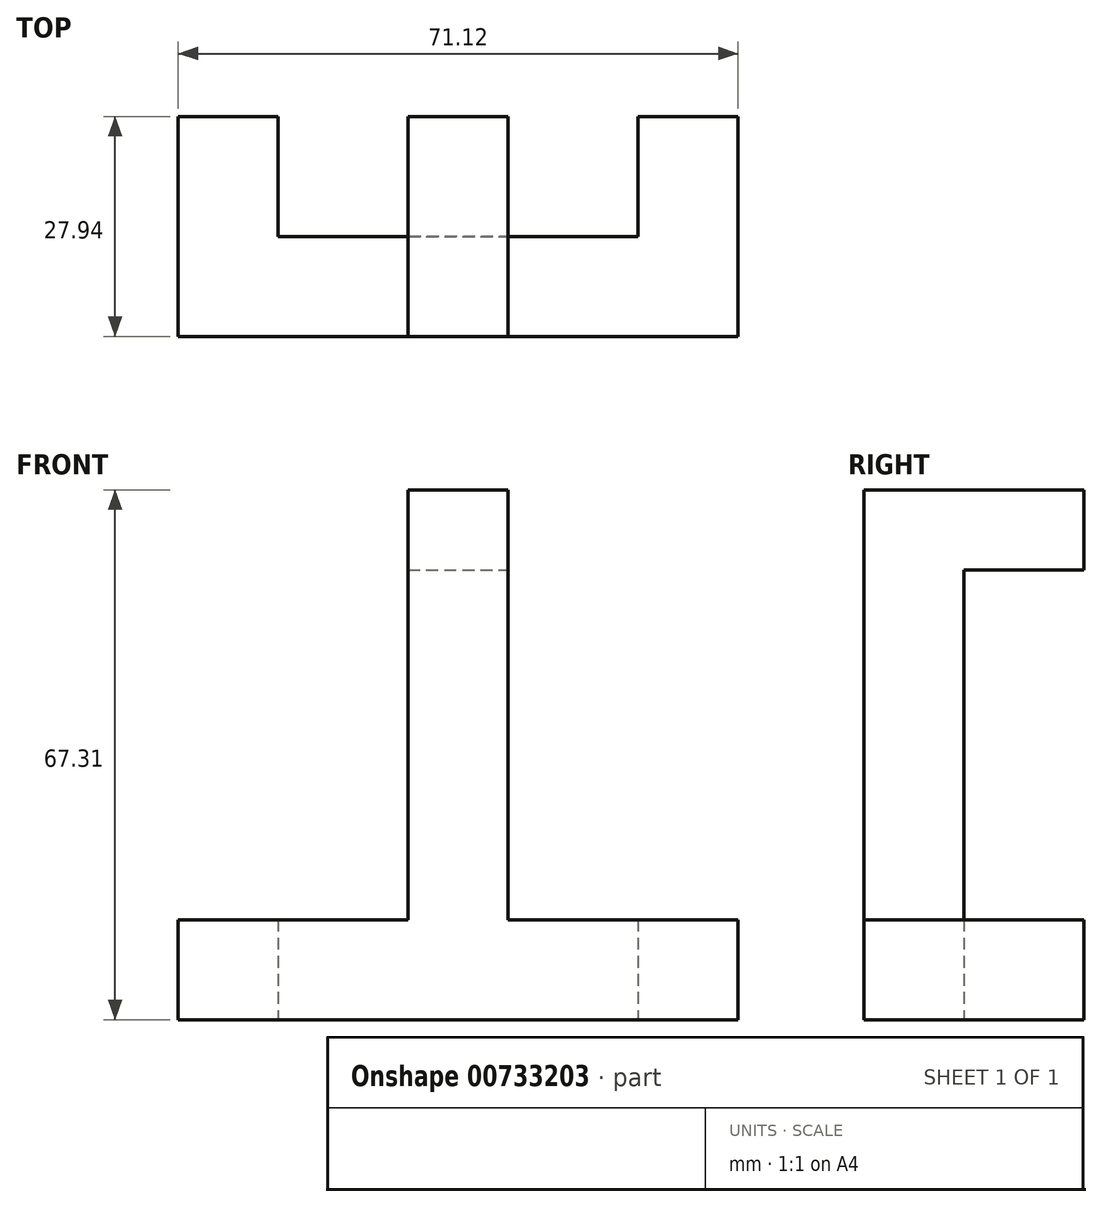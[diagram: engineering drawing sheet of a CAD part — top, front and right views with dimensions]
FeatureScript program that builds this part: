
annotation { "Feature Type Name" : "Feature", "Feature Type Description" : "" }
export const myFeature = defineFeature(function(context is Context, id is Id, definition is map)
    precondition{}
    {
        {
            var Q0;
            Q0=qCreatedBy(makeId("Front.planeOp"),FACE);
            var sketch = newSketch(context, id + "F0", { "sketchPlane" : qUnion([Q0])});
            skLineSegment(sketch, "E0.bottom", {"start": v(-13.87, 21.67) * mm, "end": v(31.85, 21.67) * mm});
            skLineSegment(sketch, "E0.top", {"start": v(-13.87, -35.48) * mm, "end": v(31.85, -35.48) * mm});
            skLineSegment(sketch, "E0.left", {"start": v(-13.87, 21.67) * mm, "end": v(-13.87, -35.48) * mm});
            skLineSegment(sketch, "E0.right", {"start": v(31.85, 21.67) * mm, "end": v(31.85, -35.48) * mm});
            skLineSegment(sketch, "E1.bottom", {"start": v(9, 21.67) * mm, "end": v(15.34, 21.67) * mm});
            skLineSegment(sketch, "E1.top", {"start": v(9, 39.45) * mm, "end": v(15.34, 39.45) * mm});
            skLineSegment(sketch, "E1.left", {"start": v(9, 21.67) * mm, "end": v(9, 39.45) * mm});
            skLineSegment(sketch, "E1.right", {"start": v(15.34, 21.67) * mm, "end": v(15.34, 39.45) * mm});
            skLineSegment(sketch, "E2.bottom", {"start": v(9, 21.67) * mm, "end": v(2.64, 21.67) * mm});
            skLineSegment(sketch, "E2.top", {"start": v(9, 39.45) * mm, "end": v(2.64, 39.45) * mm});
            skLineSegment(sketch, "E2.right", {"start": v(2.64, 21.67) * mm, "end": v(2.64, 39.45) * mm});
            skLineSegment(sketch, "E3.bottom", {"start": v(15.34, 39.45) * mm, "end": v(2.64, 39.45) * mm});
            skLineSegment(sketch, "E3.top", {"start": v(15.34, 49.61) * mm, "end": v(2.64, 49.61) * mm});
            skLineSegment(sketch, "E3.left", {"start": v(15.34, 39.45) * mm, "end": v(15.34, 49.61) * mm});
            skLineSegment(sketch, "E3.right", {"start": v(2.64, 39.45) * mm, "end": v(2.64, 49.61) * mm});
            skLineSegment(sketch, "E4.bottom", {"start": v(31.85, -35.48) * mm, "end": v(44.55, -35.48) * mm});
            skLineSegment(sketch, "E4.top", {"start": v(31.85, -17.7) * mm, "end": v(44.55, -17.7) * mm});
            skLineSegment(sketch, "E4.left", {"start": v(31.85, -35.48) * mm, "end": v(31.85, -17.7) * mm});
            skLineSegment(sketch, "E4.right", {"start": v(44.55, -35.48) * mm, "end": v(44.55, -17.7) * mm});
            skLineSegment(sketch, "E5.top", {"start": v(31.85, -5) * mm, "end": v(44.55, -5) * mm});
            skLineSegment(sketch, "E5.left", {"start": v(31.85, -17.7) * mm, "end": v(31.85, -5) * mm});
            skLineSegment(sketch, "E5.right", {"start": v(44.55, -17.7) * mm, "end": v(44.55, -5) * mm});
            skPoint(sketch, "E6.oppositeSnap0", {"position": v(38.2, -17.7) * mm});
            skLineSegment(sketch, "E6.bottom", {"start": v(-13.87, -35.48) * mm, "end": v(-26.57, -35.48) * mm});
            skLineSegment(sketch, "E6.top", {"start": v(-13.87, -17.7) * mm, "end": v(-26.57, -17.7) * mm});
            skLineSegment(sketch, "E6.left", {"start": v(-13.87, -35.48) * mm, "end": v(-13.87, -17.7) * mm});
            skLineSegment(sketch, "E6.right", {"start": v(-26.57, -35.48) * mm, "end": v(-26.57, -17.7) * mm});
            skLineSegment(sketch, "E7.top", {"start": v(-13.87, -5) * mm, "end": v(-26.57, -5) * mm});
            skLineSegment(sketch, "E7.left", {"start": v(-13.87, -17.7) * mm, "end": v(-13.87, -5) * mm});
            skLineSegment(sketch, "E7.right", {"start": v(-26.57, -17.7) * mm, "end": v(-26.57, -5) * mm});
            skLineSegment(sketch, "E8.bottom", {"start": v(-13.87, -5) * mm, "end": v(31.85, -5) * mm});
            skLineSegment(sketch, "E8.top", {"start": v(-13.87, -17.7) * mm, "end": v(31.85, -17.7) * mm});
            skLineSegment(sketch, "E8.left", {"start": v(-13.87, -5) * mm, "end": v(-13.87, -17.7) * mm});
            skLineSegment(sketch, "E8.right", {"start": v(31.85, -5) * mm, "end": v(31.85, -17.7) * mm});
            skLineSegment(sketch, "E9.bottom", {"start": v(2.64, 21.67) * mm, "end": v(15.34, 21.67) * mm});
            skLineSegment(sketch, "E9.top", {"start": v(2.64, -5) * mm, "end": v(15.34, -5) * mm});
            skLineSegment(sketch, "E9.left", {"start": v(2.64, 21.67) * mm, "end": v(2.64, -5) * mm});
            skLineSegment(sketch, "E9.right", {"start": v(15.34, 21.67) * mm, "end": v(15.34, -5) * mm});
            skLineSegment(sketch, "E10", {"start": v(31.85, -5) * mm, "end": v(31.85, 21.67) * mm});
            skSolve(sketch);
        }
        {
            var Q0;
            {var subQ0=sQuery(id+"F0.wireOp",EDGE,"E6.top");Q0=makeQuery(id+"F0.imprint","IMPRINT",FACE,{"disambiguationData":[TD([[makeQuery(id+"F0.imprint","IMPRINT",EDGE,{"derivedFrom":subQ0}),-1.0]])]});}
            var Q1;
            {var subQ0=sQuery(id+"F0.wireOp",EDGE,"E4.top");Q1=makeQuery(id+"F0.imprint","IMPRINT",FACE,{"disambiguationData":[TD([[makeQuery(id+"F0.imprint","IMPRINT",EDGE,{"derivedFrom":subQ0}),1.0]])]});}
            var Q2;
            {var subQ4=sQuery(id+"F0.wireOp",EDGE,"E8.top");Q2=makeQuery(id+"F0.imprint","IMPRINT",FACE,{"disambiguationData":[TD([[makeQuery(id+"F0.imprint","IMPRINT",EDGE,{"derivedFrom":subQ4}),1.0]])]});}
            var Q3;
            {var subQ2=sQuery(id+"F0.wireOp",EDGE,"E9.left");Q3=makeQuery(id+"F0.imprint","IMPRINT",FACE,{"disambiguationData":[TD([[makeQuery(id+"F0.imprint","IMPRINT",EDGE,{"derivedFrom":subQ2}),1.0]])]});}
            var Q4;
            Q4=makeQuery(id+"F0.imprint","IMPRINT",FACE,{"disambiguationData":[TD([[makeQuery(id+"F0.imprint","IMPRINT",EDGE,{"derivedFrom":sQuery(id+"F0.wireOp",EDGE,"E1.top")}),-1.0]])]});
            var Q5;
            {var subQ0=sQuery(id+"F0.wireOp",EDGE,"E1.left");Q5=makeQuery(id+"F0.imprint","IMPRINT",FACE,{"disambiguationData":[TD([[makeQuery(id+"F0.imprint","IMPRINT",EDGE,{"derivedFrom":subQ0}),1.0]])]});}
            var Q6;
            Q6=makeQuery(id+"F0.imprint","IMPRINT",FACE,{"disambiguationData":[TD([[makeQuery(id+"F0.imprint","IMPRINT",EDGE,{"derivedFrom":sQuery(id+"F0.wireOp",EDGE,"E1.top")}),1.0]])]});
            extrude(context, id + "F1", {"entities" : qUnion([Q0, Q1, Q2, Q3, Q4, Q5, Q6]), "depth" : 12.7 * mm, "offsetDistance" : 25.4 * mm});
        }
        {
            var Q0;
            Q0=makeQuery(id+"F0.imprint","IMPRINT",FACE,{"disambiguationData":[TD([[makeQuery(id+"F0.imprint","IMPRINT",EDGE,{"derivedFrom":sQuery(id+"F0.wireOp",EDGE,"E1.top")}),1.0]])]});
            var Q1;
            {var subQ0=sQuery(id+"F0.wireOp",EDGE,"E6.top");Q1=makeQuery(id+"F0.imprint","IMPRINT",FACE,{"disambiguationData":[TD([[makeQuery(id+"F0.imprint","IMPRINT",EDGE,{"derivedFrom":subQ0}),-1.0]])]});}
            var Q2;
            {var subQ0=sQuery(id+"F0.wireOp",EDGE,"E4.top");Q2=makeQuery(id+"F0.imprint","IMPRINT",FACE,{"disambiguationData":[TD([[makeQuery(id+"F0.imprint","IMPRINT",EDGE,{"derivedFrom":subQ0}),1.0]])]});}
            extrude(context, id + "F2", {"entities" : qUnion([Q0, Q1, Q2]), "operationType" : NewBodyOperationType.ADD, "oppositeDirection" : true, "depth" : 15.24 * mm, "offsetDistance" : 25.4 * mm});
        }
    });
